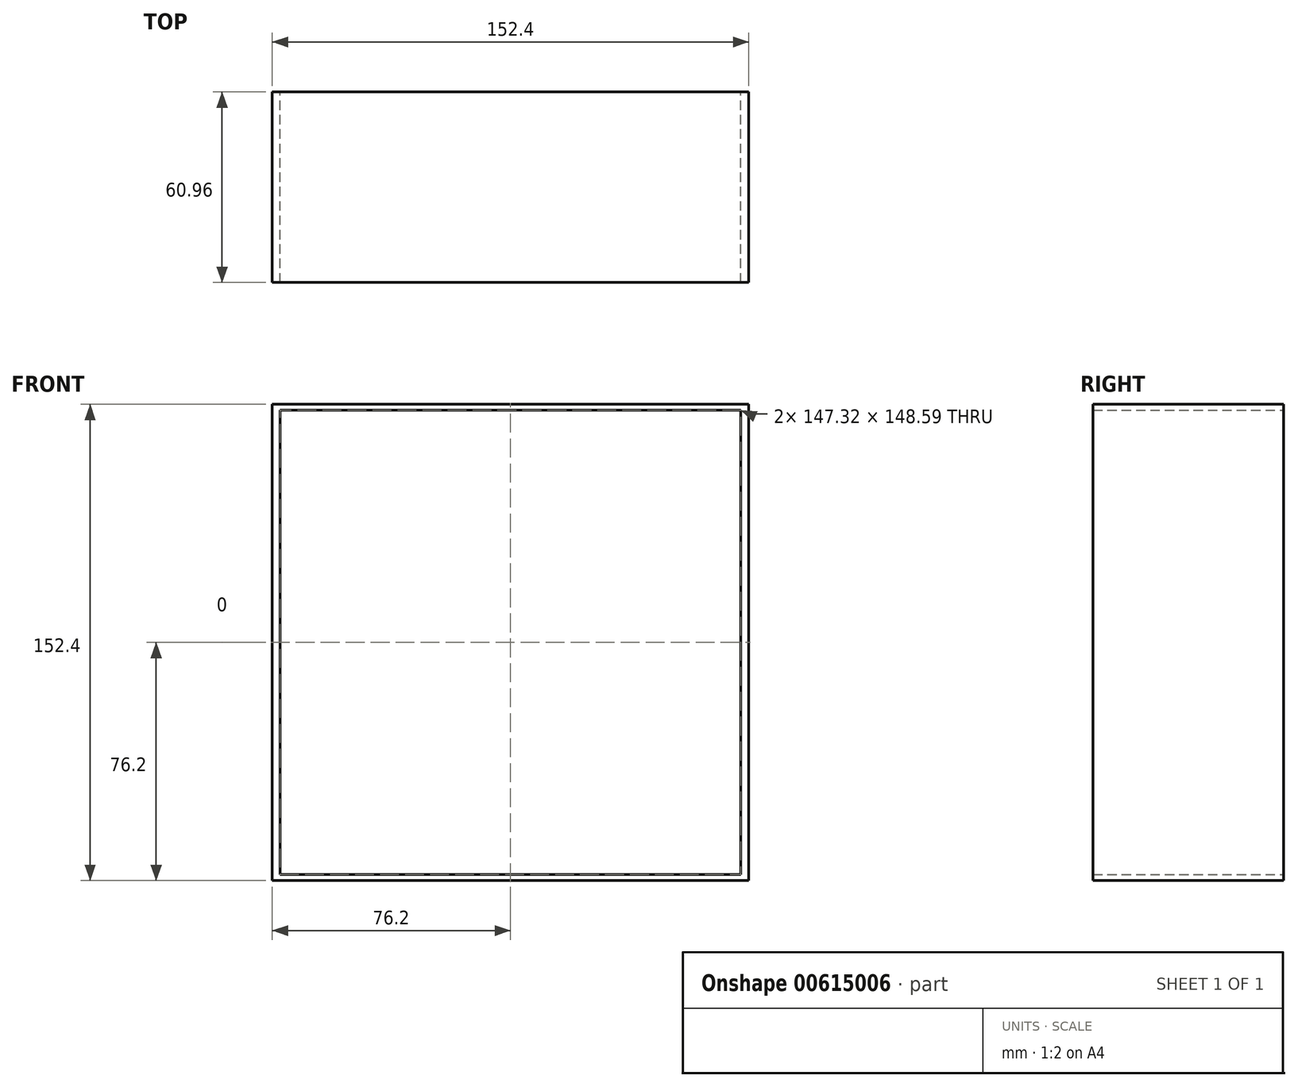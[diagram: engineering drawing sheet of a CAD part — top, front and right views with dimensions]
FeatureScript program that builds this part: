
annotation { "Feature Type Name" : "Feature", "Feature Type Description" : "" }
export const myFeature = defineFeature(function(context is Context, id is Id, definition is map)
    precondition{}
    {
        {
            var Q0;
            Q0=qCreatedBy(makeId("Front.planeOp"),FACE);
            var sketch = newSketch(context, id + "F0", { "sketchPlane" : qUnion([Q0])});
            skLineSegment(sketch, "E0.bottom", {"start": v(76.2, -76.2) * mm, "end": v(-76.2, -76.2) * mm});
            skLineSegment(sketch, "E0.top", {"start": v(76.2, 76.2) * mm, "end": v(-76.2, 76.2) * mm});
            skLineSegment(sketch, "E0.left", {"start": v(76.2, -76.2) * mm, "end": v(76.2, 76.2) * mm});
            skLineSegment(sketch, "E0.right", {"start": v(-76.2, -76.2) * mm, "end": v(-76.2, 76.2) * mm});
            skPoint(sketch, "E0.middle", {"position": v(0, 0) * mm});
            skLineSegment(sketch, "E1.bottom", {"start": v(73.66, -74.3) * mm, "end": v(-73.66, -74.3) * mm});
            skLineSegment(sketch, "E1.top", {"start": v(73.66, 74.3) * mm, "end": v(-73.66, 74.3) * mm});
            skLineSegment(sketch, "E1.left", {"start": v(73.66, -74.3) * mm, "end": v(73.66, 74.3) * mm});
            skLineSegment(sketch, "E1.right", {"start": v(-73.66, -74.3) * mm, "end": v(-73.66, 74.3) * mm});
            skSolve(sketch);
        }
        {
            var Q0;
            Q0 = qSketchRegion(id + "F0", true);
            extrude(context, id + "F1", {"entities" : qUnion([Q0]), "depth" : 60.96 * mm, "offsetDistance" : 25.4 * mm});
        }
    });
